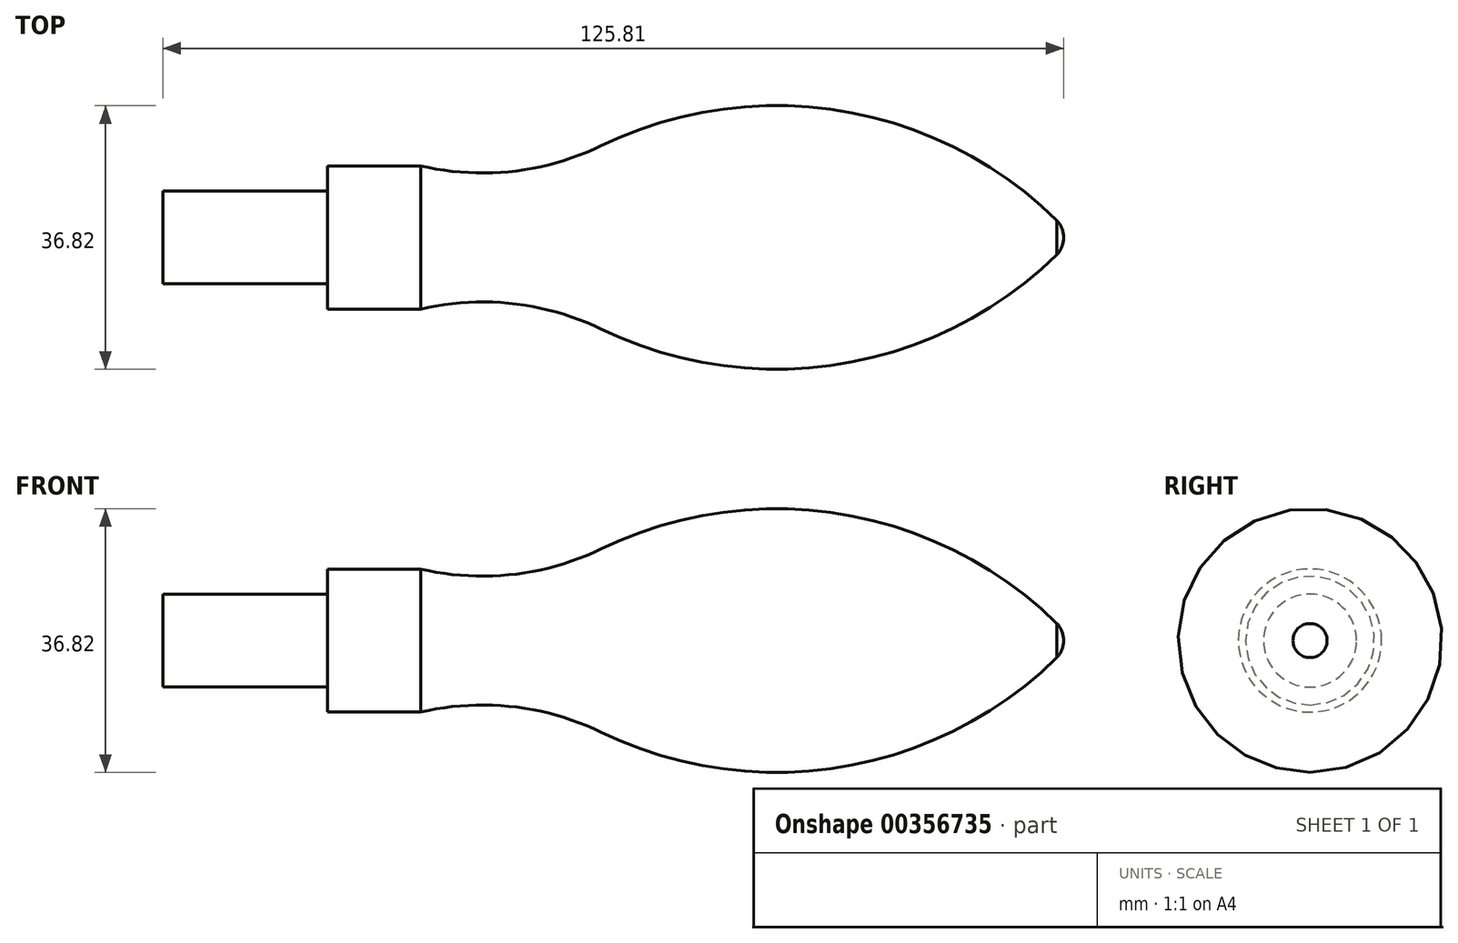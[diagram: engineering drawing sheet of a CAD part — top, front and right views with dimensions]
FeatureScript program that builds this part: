
annotation { "Feature Type Name" : "Feature", "Feature Type Description" : "" }
export const myFeature = defineFeature(function(context is Context, id is Id, definition is map)
    precondition{}
    {
        {
            var Q0;
            Q0=qCreatedBy(makeId("Top.planeOp"),FACE);
            var sketch = newSketch(context, id + "F0", { "sketchPlane" : qUnion([Q0])});
            skArc(sketch, "E0", {"start": v(39.23, 2.38) * mm, "mid": v(9.05, 17.68) * mm, "end": v(-24.42, 12.8) * mm});
            skArc(sketch, "E1", {"start": v(40.16, 0) * mm, "mid": v(39.85, 1.44) * mm, "end": v(38.97, 2.63) * mm});
            skLineSegment(sketch, "E2", {"start": v(-85.65, 0) * mm, "end": v(-85.65, 6.5) * mm});
            skLineSegment(sketch, "E3", {"start": v(-85.65, 6.5) * mm, "end": v(-62.65, 6.5) * mm});
            skLineSegment(sketch, "E4", {"start": v(-62.65, 0) * mm, "end": v(-62.65, 10) * mm});
            skLineSegment(sketch, "E5", {"start": v(-62.65, 10) * mm, "end": v(-49.65, 10) * mm});
            skArc(sketch, "E6", {"start": v(-49.65, 10) * mm, "mid": v(-36.8, 9.23) * mm, "end": v(-24.42, 12.8) * mm});
            skPoint(sketch, "E7", {"position": v(40.16, 0) * mm});
            skLineSegment(sketch, "E8.MirrorCS", {"start": v(-85.65, 0) * mm, "end": v(-85.65, -6.5) * mm});
            skLineSegment(sketch, "E9.MirrorCS", {"start": v(-85.65, -6.5) * mm, "end": v(-62.65, -6.5) * mm});
            skLineSegment(sketch, "E10.MirrorCS", {"start": v(-62.65, 0) * mm, "end": v(-62.65, -10) * mm});
            skLineSegment(sketch, "E11.MirrorCS", {"start": v(-62.65, -10) * mm, "end": v(-49.65, -10) * mm});
            skArc(sketch, "E12.MirrorCS", {"start": v(-49.65, -10) * mm, "mid": v(-36.8, -9.23) * mm, "end": v(-24.42, -12.8) * mm});
            skArc(sketch, "E13.MirrorCS", {"start": v(39.23, -2.38) * mm, "mid": v(9.05, -17.68) * mm, "end": v(-24.42, -12.8) * mm});
            skArc(sketch, "E14.MirrorCS", {"start": v(40.16, 0) * mm, "mid": v(39.85, -1.44) * mm, "end": v(38.97, -2.63) * mm});
            skLineSegment(sketch, "E15", {"start": v(64.67, 0) * mm, "end": v(-115.33, 0) * mm});
            skSolve(sketch);
        }
        {
            var Q0;
            {var subQ1=sQuery(id+"F0.wireOp",EDGE,"E11.MirrorCS");Q0=makeQuery(id+"F0.imprint","IMPRINT",FACE,{"disambiguationData":[TD([[makeQuery(id+"F0.imprint","IMPRINT",EDGE,{"derivedFrom":subQ1}),1.0]])]});}
            var Q1;
            {var subQ0=sQuery(id+"F0.wireOp",EDGE,"E8.MirrorCS");Q1=makeQuery(id+"F0.imprint","IMPRINT",FACE,{"disambiguationData":[TD([[makeQuery(id+"F0.imprint","IMPRINT",EDGE,{"derivedFrom":subQ0}),1.0]])]});}
            var Q2;
            Q2=sQuery(id+"F0.wireOp",EDGE,"E15");
            revolve(context, id + "F1", {"entities" : qUnion([Q0, Q1]), "axis" : qUnion([Q2]), "revolveType" : RevolveType.FULL});
        }
    });
